# Revit family: Specialty_Equipment-Planter-Planters_Unlimited-Madera-Tapered-Square-Rectangular
name_source: partatom
category: Specialty Equipment
units: mm (PartAtom-declared; Revit-internal decimal feet)

## family parameters
Always vertical = Yes
Cut with Voids When Loaded = No
Enable Cutting in Views = Yes
Maintain Annotation Orientation = No
OmniClass Number = 23.40.05.21.17
OmniClass Title = Planters
Part Type = Normal
Room Calculation Point = No
Round Connector Dimension = Use Diameter
Shared = No
Work Plane-Based = No

## types (1)
- Default - Load Type Catalog
    Assembly Code = G2050600
    CD_Height = 18"
    CD_Height Max = 60"
    CD_Height Min = 18"
    CD_Length = 18"
    CD_Length Max = 120"
    CD_Length Min = 18"
    CD_Offset = 0"
    CD_Product Name = Madera Planter
    CD_Product Page URL = https://www.plantersunlimited.com
    CD_Requested Height = 18"
    CD_Requested Length = 18"
    CD_Requested Length Bottom = 12"
    CD_Requested Width = 15"
    CD_Requested Width Bottom = 10"
    CD_Specification = https://www.plantersunlimited.com
    CD_Stiffener Bottom Length = 13 7/8"
    CD_Stiffener Bottom Width = 11 1/2"
    CD_Stiffener Top Length = 15 5/8"
    CD_Stiffener Top Width = 13"
    CD_Width = 15"
    CD_Width Max = 72"
    CD_Width Min = 15"
    Default Elevation = 0"
    Description = Modular Planting Bed
    Manufacturer = Planters Unlimited
    Material = Plastic-Fiberglass-Carlsbad-Faux Wood-Grey
    Model = Madera Series Planters
    Rectangle Planter = Yes
    Square Planter = No
    Type Comments = Rectangular/Square Tapered Planter
    URL = https://www.plantersunlimited.com

## geometry (parser evidence)
native form markers: Extrusion x1, Sweep x3
no freeform markers — native parametric forms only
